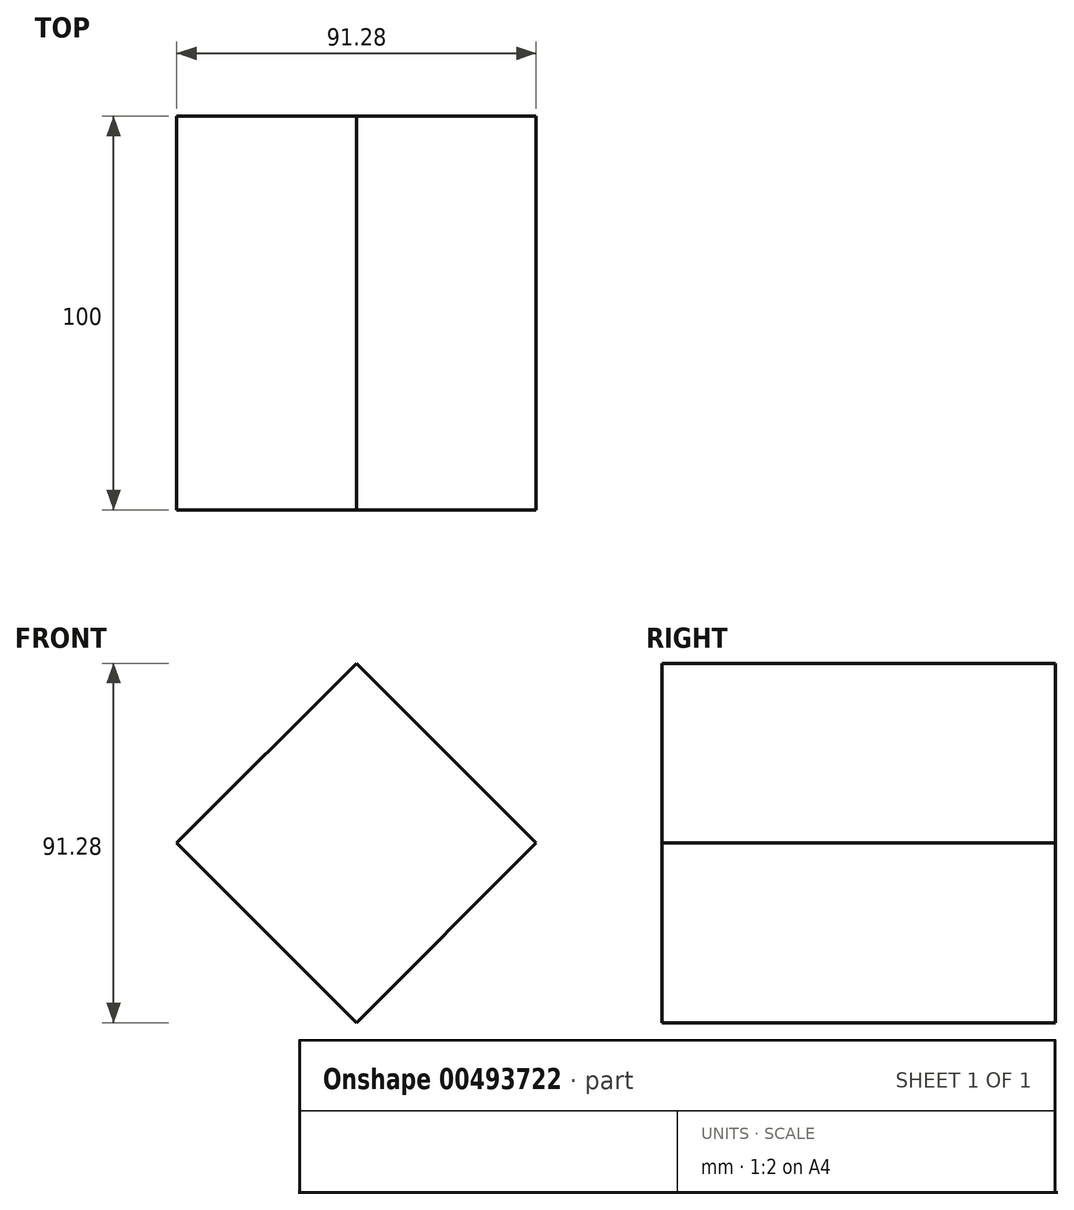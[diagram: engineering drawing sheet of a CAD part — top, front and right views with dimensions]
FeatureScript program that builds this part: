
annotation { "Feature Type Name" : "Feature", "Feature Type Description" : "" }
export const myFeature = defineFeature(function(context is Context, id is Id, definition is map)
    precondition{}
    {
        {
            var Q0;
            Q0=qCreatedBy(makeId("Front.planeOp"),FACE);
            var sketch = newSketch(context, id + "F0", { "sketchPlane" : qUnion([Q0])});
            skCircle(sketch, "E0.cCircle", {"center": v(0, 0) * mm, "radius": 45.64 * mm, "construction": true});
            skLineSegment(sketch, "E0.0", {"start": v(45.64, 0) * mm, "end": v(0, -45.64) * mm});
            skLineSegment(sketch, "E0.1", {"start": v(0, -45.64) * mm, "end": v(-45.64, 0) * mm});
            skLineSegment(sketch, "E0.2", {"start": v(-45.64, 0) * mm, "end": v(0, 45.64) * mm});
            skLineSegment(sketch, "E0.3", {"start": v(0, 45.64) * mm, "end": v(45.64, 0) * mm});
            skSolve(sketch);
        }
        {
            var Q0;
            Q0=makeQuery(id+"F0.imprint","IMPRINT",FACE,{"disambiguationData":[TD([[makeQuery(id+"F0.imprint","IMPRINT",EDGE,{"derivedFrom":sQuery(id+"F0.wireOp",EDGE,"E0.0")}),-1.0]])]});
            extrude(context, id + "F1", {"entities" : qUnion([Q0]), "endBound" : BoundingType.SYMMETRIC, "depth" : 100 * mm});
        }
    });
